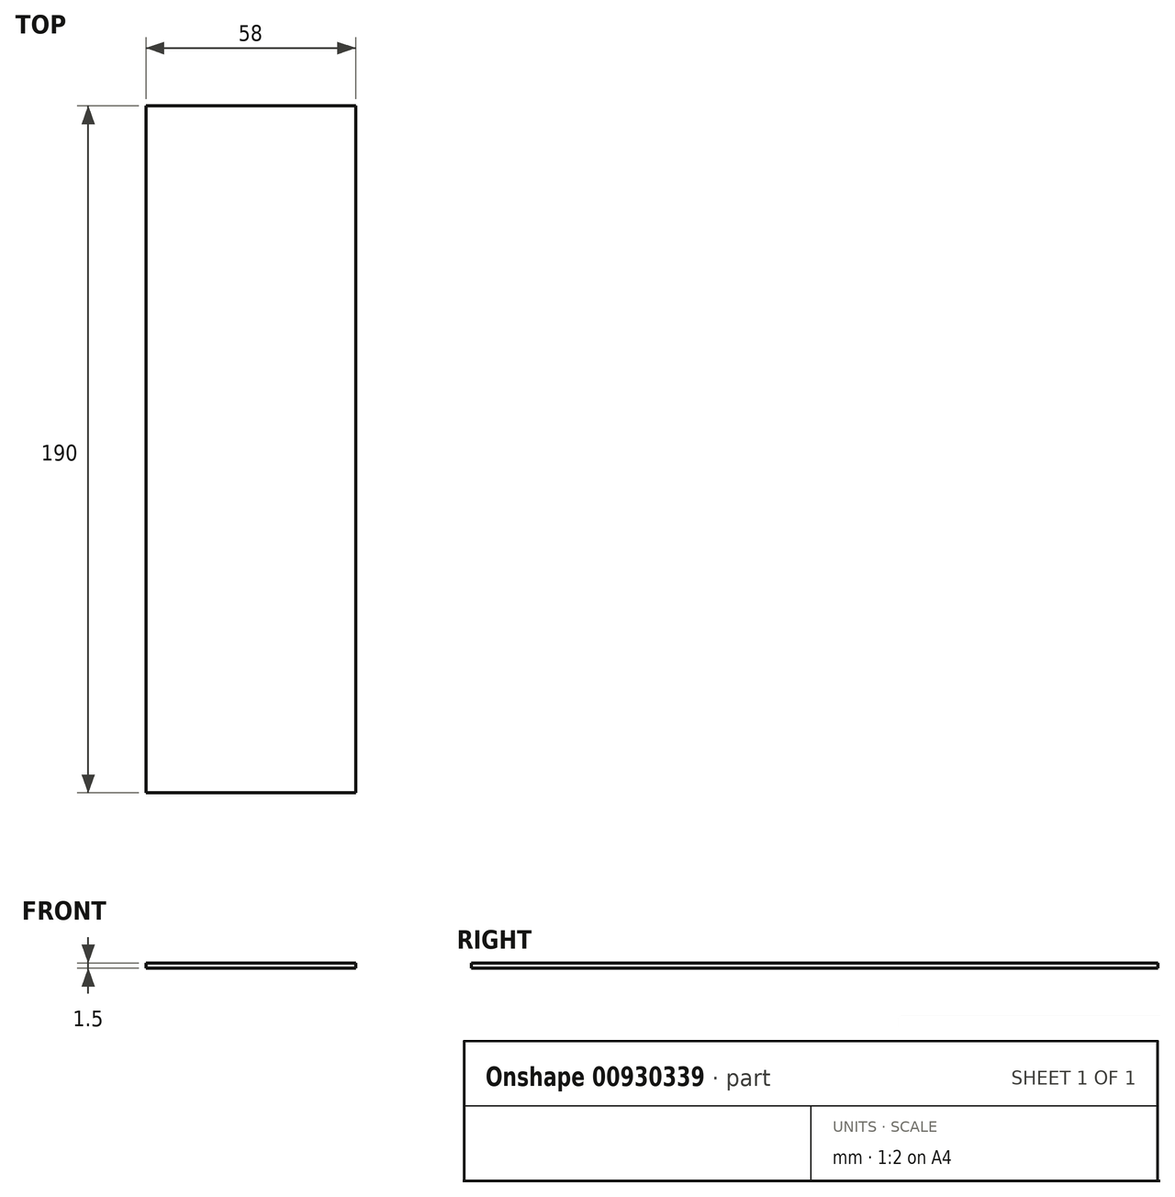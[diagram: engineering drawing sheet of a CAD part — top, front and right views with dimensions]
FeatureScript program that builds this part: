
annotation { "Feature Type Name" : "Feature", "Feature Type Description" : "" }
export const myFeature = defineFeature(function(context is Context, id is Id, definition is map)
    precondition{}
    {
        {
            var Q0;
            Q0=qCreatedBy(makeId("Top.planeOp"),FACE);
            var sketch = newSketch(context, id + "F0", { "sketchPlane" : qUnion([Q0])});
            skLineSegment(sketch, "E0.bottom", {"start": v(29, 95) * mm, "end": v(-29, 95) * mm});
            skLineSegment(sketch, "E0.top", {"start": v(29, -95) * mm, "end": v(-29, -95) * mm});
            skLineSegment(sketch, "E0.left", {"start": v(29, 95) * mm, "end": v(29, -95) * mm});
            skLineSegment(sketch, "E0.right", {"start": v(-29, 95) * mm, "end": v(-29, -95) * mm});
            skPoint(sketch, "E0.middle", {"position": v(0, 0) * mm});
            skSolve(sketch);
        }
        {
            var Q0;
            Q0 = qSketchRegion(id + "F0", true);
            extrude(context, id + "F1", {"entities" : qUnion([Q0]), "depth" : 1.5 * mm, "offsetDistance" : 25 * mm});
        }
    });
